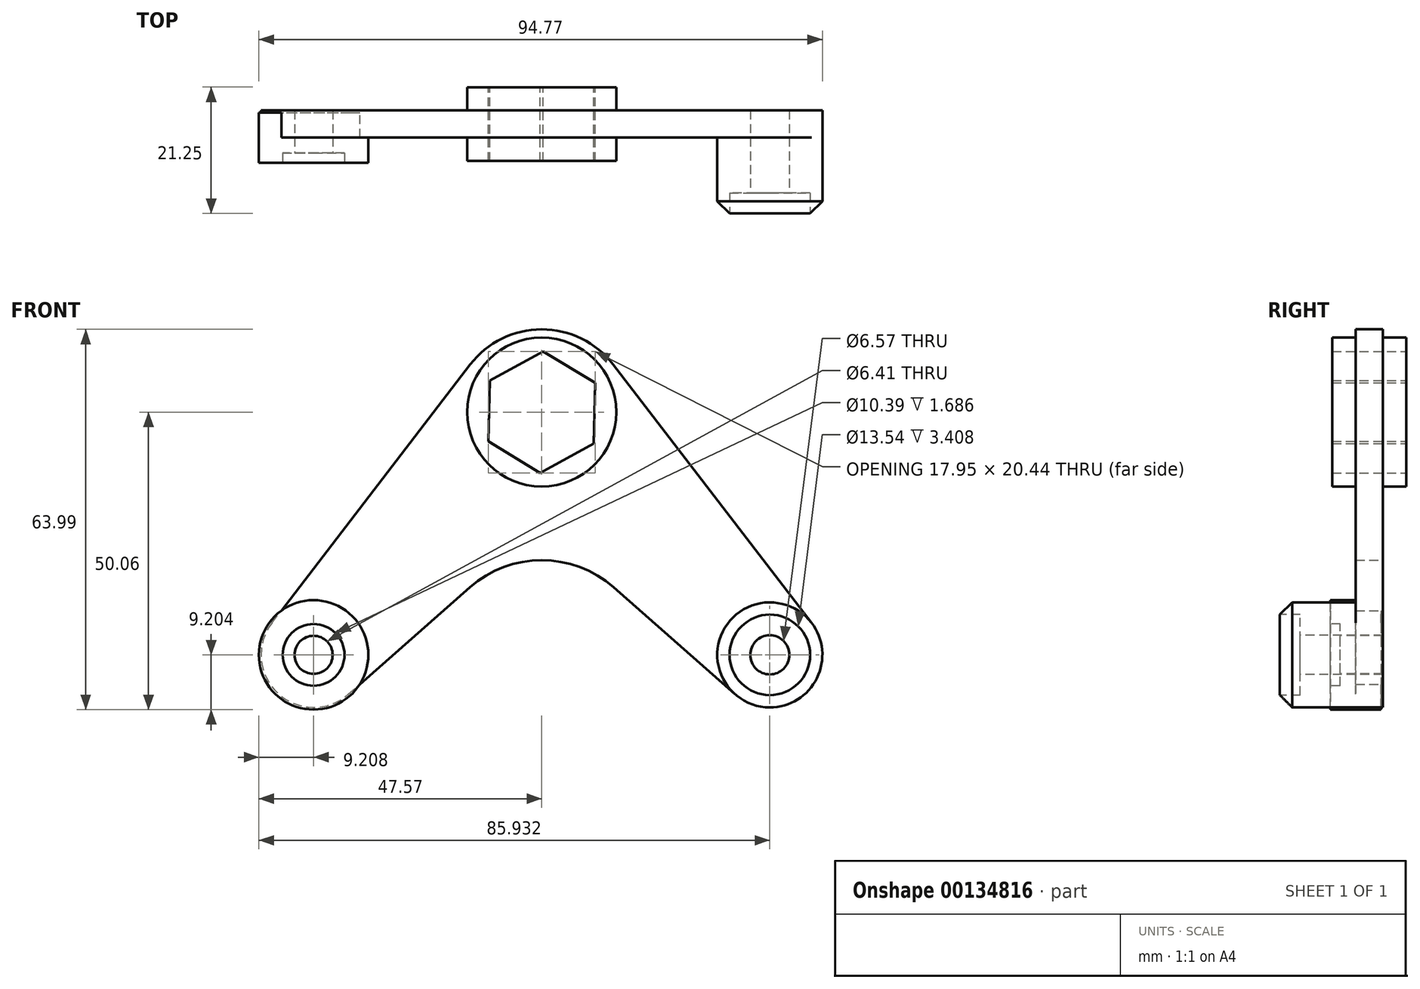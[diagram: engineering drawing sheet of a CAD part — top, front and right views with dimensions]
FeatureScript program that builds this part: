
annotation { "Feature Type Name" : "Feature", "Feature Type Description" : "" }
export const myFeature = defineFeature(function(context is Context, id is Id, definition is map)
    precondition{}
    {
        {
            var Q0;
            Q0=qCreatedBy(makeId("Front.planeOp"),FACE);
            var sketch = newSketch(context, id + "F0", { "sketchPlane" : qUnion([Q0])});
            skCircle(sketch, "E0", {"center": v(0, 0) * mm, "radius": 12.54 * mm});
            skSolve(sketch);
        }
        {
            var Q0;
            Q0 = qSketchRegion(id + "F0", true);
            extrude(context, id + "F1", {"entities" : qUnion([Q0]), "endBound" : BoundingType.SYMMETRIC, "depth" : 12.43 * mm});
        }
        {
            var Q0;
            Q0=makeQuery(id+"F1.opExtrude","CAP_FACE",FACE,{"disambiguationData":[OSD([sQuery(id+"F0.wireOp",EDGE,"E0")])],"isStart":false});
            var sketch = newSketch(context, id + "F2", { "sketchPlane" : qUnion([Q0])});
            skCircle(sketch, "E1.cCircle", {"center": v(0, 0) * mm, "radius": 7.38 * mm, "construction": true});
            skLineSegment(sketch, "E1.0", {"start": v(-8.03, 2.83) * mm, "end": v(-1.57, 8.37) * mm});
            skLineSegment(sketch, "E1.1", {"start": v(-1.57, 8.37) * mm, "end": v(6.47, 5.54) * mm});
            skLineSegment(sketch, "E1.2", {"start": v(6.47, 5.54) * mm, "end": v(8.03, -2.83) * mm});
            skLineSegment(sketch, "E1.3", {"start": v(8.03, -2.83) * mm, "end": v(1.57, -8.37) * mm});
            skLineSegment(sketch, "E1.4", {"start": v(1.57, -8.37) * mm, "end": v(-6.47, -5.54) * mm});
            skLineSegment(sketch, "E1.5", {"start": v(-6.47, -5.54) * mm, "end": v(-8.03, 2.83) * mm});
            skPoint(sketch, "E1.0.midPoint", {"position": v(-4.8, 5.6) * mm});
            skSolve(sketch);
        }
        {
            var Q0;
            Q0 = qSketchRegion(id + "F2", true);
            extrude(context, id + "F3", {"entities" : qUnion([Q0]), "operationType" : NewBodyOperationType.REMOVE, "oppositeDirection" : true, "depth" : 43.1 * mm});
        }
        {
            var Q0;
            Q0=qCreatedBy(makeId("Front.planeOp"),FACE);
            var sketch = newSketch(context, id + "F4", { "sketchPlane" : qUnion([Q0])});
            skCircle(sketch, "E2", {"center": v(-38.36, -40.86) * mm, "radius": 8.84 * mm});
            skCircle(sketch, "E3.MirrorC", {"center": v(38.36, -40.86) * mm, "radius": 8.84 * mm});
            skLineSegment(sketch, "E4", {"start": v(-45.37, -35.48) * mm, "end": v(-12, 8) * mm});
            skLineSegment(sketch, "E5.MirrorCS", {"start": v(45.37, -35.48) * mm, "end": v(12, 8) * mm});
            skLineSegment(sketch, "E6", {"start": v(-32.52, -47.49) * mm, "end": v(-12.1, -29.5) * mm});
            skLineSegment(sketch, "E7.MirrorCS", {"start": v(32.52, -47.49) * mm, "end": v(12.1, -29.5) * mm});
            skArc(sketch, "E8", {"start": v(12.1, -29.5) * mm, "mid": v(0, -24.92) * mm, "end": v(-12.1, -29.5) * mm});
            skArc(sketch, "E9", {"start": v(12, 8) * mm, "mid": v(0, 13.93) * mm, "end": v(-12, 8) * mm});
            skSolve(sketch);
        }
        {
            var Q0;
            Q0 = qSketchRegion(id + "F4", true);
            extrude(context, id + "F5", {"entities" : qUnion([Q0]), "operationType" : NewBodyOperationType.ADD, "endBound" : BoundingType.SYMMETRIC, "depth" : 4.58 * mm});
        }
        {
            var Q0;
            {var subQ0=sQuery(id+"F4.wireOp",EDGE,"E3.MirrorC");var subQ1=sQuery(id+"F4.wireOp",EDGE,"E4");var subQ2=sQuery(id+"F4.wireOp",EDGE,"E2");var subQ3=sQuery(id+"F4.wireOp",EDGE,"E8");var subQ4=sQuery(id+"F4.wireOp",EDGE,"E5.MirrorCS");var subQ5=sQuery(id+"F4.wireOp",EDGE,"E6");var subQ6=sQuery(id+"F4.wireOp",EDGE,"E9");var subQ7=sQuery(id+"F4.wireOp",EDGE,"E7.MirrorCS");Q0=makeQuery(id+"F5.boolean.opBoolean","SPLIT",FACE,{"disambiguationData":[TD([makeQuery(id+"F1.opExtrude","SWEPT_FACE",FACE,{"disambiguationData":[OSD([sQuery(id+"F0.wireOp",EDGE,"E0")])]})])],"derivedFrom":makeQuery(id+"F5.opExtrude","CAP_FACE",FACE,{"disambiguationData":[OSD([subQ2,subQ0,subQ1,subQ4,subQ5,subQ7,subQ3,subQ6])],"isStart":false})});}
            var sketch = newSketch(context, id + "F6", { "sketchPlane" : qUnion([Q0])});
            skCircle(sketch, "E10", {"center": v(-38.36, -40.86) * mm, "radius": 9.2 * mm});
            skSolve(sketch);
        }
        {
            var Q0;
            Q0 = qSketchRegion(id + "F6", true);
            extrude(context, id + "F7", {"entities" : qUnion([Q0]), "operationType" : NewBodyOperationType.ADD, "endBound" : BoundingType.SYMMETRIC, "depth" : 8.5 * mm});
        }
        {
            var Q0;
            {var subQ0=sQuery(id+"F4.wireOp",EDGE,"E3.MirrorC");var subQ1=sQuery(id+"F4.wireOp",EDGE,"E4");var subQ2=sQuery(id+"F4.wireOp",EDGE,"E2");var subQ3=sQuery(id+"F4.wireOp",EDGE,"E8");var subQ4=sQuery(id+"F4.wireOp",EDGE,"E5.MirrorCS");var subQ5=sQuery(id+"F4.wireOp",EDGE,"E6");var subQ6=sQuery(id+"F4.wireOp",EDGE,"E9");var subQ7=sQuery(id+"F4.wireOp",EDGE,"E7.MirrorCS");Q0=makeQuery(id+"F5.boolean.opBoolean","SPLIT",FACE,{"disambiguationData":[TD([makeQuery(id+"F1.opExtrude","SWEPT_FACE",FACE,{"disambiguationData":[OSD([sQuery(id+"F0.wireOp",EDGE,"E0")])]})])],"derivedFrom":makeQuery(id+"F5.opExtrude","CAP_FACE",FACE,{"disambiguationData":[OSD([subQ2,subQ0,subQ1,subQ4,subQ5,subQ7,subQ3,subQ6])],"isStart":false})});}
            var sketch = newSketch(context, id + "F8", { "sketchPlane" : qUnion([Q0])});
            skCircle(sketch, "E11", {"center": v(38.36, -40.86) * mm, "radius": 8.84 * mm});
            skSolve(sketch);
        }
        {
            var Q0;
            Q0 = qSketchRegion(id + "F8", true);
            extrude(context, id + "F9", {"entities" : qUnion([Q0]), "operationType" : NewBodyOperationType.ADD, "depth" : 13.21 * mm});
        }
        {
            var Q0;
            Q0=makeQuery(id+"F7.opExtrude","CAP_FACE",FACE,{"disambiguationData":[OSD([sQuery(id+"F6.wireOp",EDGE,"E10")])],"isStart":false});
            var sketch = newSketch(context, id + "F10", { "sketchPlane" : qUnion([Q0])});
            skCircle(sketch, "E12", {"center": v(-38.36, -40.86) * mm, "radius": 3.2 * mm});
            skSolve(sketch);
        }
        {
            var Q0;
            Q0 = qSketchRegion(id + "F10", true);
            extrude(context, id + "F11", {"entities" : qUnion([Q0]), "operationType" : NewBodyOperationType.REMOVE, "oppositeDirection" : true, "depth" : 28.8 * mm});
        }
        {
            var Q0;
            Q0=makeQuery(id+"F7.opExtrude","CAP_FACE",FACE,{"disambiguationData":[OSD([sQuery(id+"F6.wireOp",EDGE,"E10")])],"isStart":false});
            var sketch = newSketch(context, id + "F12", { "sketchPlane" : qUnion([Q0])});
            skCircle(sketch, "E13", {"center": v(-38.36, -40.86) * mm, "radius": 5.2 * mm});
            skSolve(sketch);
        }
        {
            var Q0;
            Q0 = qSketchRegion(id + "F12", true);
            extrude(context, id + "F13", {"entities" : qUnion([Q0]), "operationType" : NewBodyOperationType.REMOVE, "oppositeDirection" : true, "depth" : 1.69 * mm});
        }
        {
            var Q0;
            Q0=makeQuery(id+"F9.opExtrude","CAP_FACE",FACE,{"disambiguationData":[OSD([sQuery(id+"F8.wireOp",EDGE,"E11")])],"isStart":false});
            var sketch = newSketch(context, id + "F14", { "sketchPlane" : qUnion([Q0])});
            skCircle(sketch, "E14", {"center": v(38.36, -40.86) * mm, "radius": 3.29 * mm});
            skSolve(sketch);
        }
        {
            var Q0;
            Q0 = qSketchRegion(id + "F14", true);
            extrude(context, id + "F15", {"entities" : qUnion([Q0]), "operationType" : NewBodyOperationType.REMOVE, "oppositeDirection" : true, "depth" : 33.08 * mm});
        }
        {
            var Q0;
            Q0=makeQuery(id+"F9.opExtrude","CAP_FACE",FACE,{"disambiguationData":[OSD([sQuery(id+"F8.wireOp",EDGE,"E11")])],"isStart":false});
            var sketch = newSketch(context, id + "F16", { "sketchPlane" : qUnion([Q0])});
            skCircle(sketch, "E15", {"center": v(38.36, -40.86) * mm, "radius": 6.77 * mm});
            skSolve(sketch);
        }
        {
            var Q0;
            Q0 = qSketchRegion(id + "F16", true);
            extrude(context, id + "F17", {"entities" : qUnion([Q0]), "operationType" : NewBodyOperationType.REMOVE, "oppositeDirection" : true, "depth" : 3.88 * mm});
        }
        {
            var Q0;
            Q0=makeQuery(id+"F9.opExtrude","CAP_EDGE",EDGE,{"disambiguationData":[OSD([sQuery(id+"F8.wireOp",EDGE,"E11")])],"isStart":false});
            chamfer(context, id + "F18", {"entities" : qUnion([Q0]), "width" : 2.54 * mm, "tangentPropagation" : true});
        }
        {
            var Q0;
            Q0=makeQuery(id+"F5.boolean.opBoolean","SPLIT",FACE,{"disambiguationData":[TD([makeQuery(id+"F3.boolean.opBoolean","COPY",FACE,{"derivedFrom":makeQuery(id+"F3.opExtrude","SWEPT_FACE",FACE,{"disambiguationData":[OSD([sQuery(id+"F2.wireOp",EDGE,"E1.0")])]})})])],"derivedFrom":makeQuery(id+"F5.opExtrude","CAP_FACE",FACE,{"disambiguationData":[OSD([sQuery(id+"F4.wireOp",EDGE,"E2"),sQuery(id+"F4.wireOp",EDGE,"E3.MirrorC"),sQuery(id+"F4.wireOp",EDGE,"E4"),sQuery(id+"F4.wireOp",EDGE,"E5.MirrorCS"),sQuery(id+"F4.wireOp",EDGE,"E6"),sQuery(id+"F4.wireOp",EDGE,"E7.MirrorCS"),sQuery(id+"F4.wireOp",EDGE,"E8"),sQuery(id+"F4.wireOp",EDGE,"E9")])],"isStart":false})});
            var sketch = newSketch(context, id + "F19", { "sketchPlane" : qUnion([Q0])});
            skCircle(sketch, "E16.cCircle", {"center": v(0, 0) * mm, "radius": 7.5 * mm, "construction": true});
            skLineSegment(sketch, "E16.0", {"start": v(7.5, 4.33) * mm, "end": v(7.5, -4.33) * mm});
            skLineSegment(sketch, "E16.1", {"start": v(7.5, -4.33) * mm, "end": v(0, -8.67) * mm});
            skLineSegment(sketch, "E16.2", {"start": v(0, -8.67) * mm, "end": v(-7.5, -4.33) * mm});
            skLineSegment(sketch, "E16.3", {"start": v(-7.5, -4.33) * mm, "end": v(-7.5, 4.33) * mm});
            skLineSegment(sketch, "E16.4", {"start": v(-7.5, 4.33) * mm, "end": v(0, 8.67) * mm});
            skLineSegment(sketch, "E16.5", {"start": v(0, 8.67) * mm, "end": v(7.5, 4.33) * mm});
            skPoint(sketch, "E16.0.midPoint", {"position": v(7.5, 0) * mm});
            skSolve(sketch);
        }
        {
            var Q0;
            Q0 = qSketchRegion(id + "F19", true);
            extrude(context, id + "F20", {"entities" : qUnion([Q0]), "operationType" : NewBodyOperationType.REMOVE, "oppositeDirection" : true, "depth" : 42.8 * mm});
        }
        {
            var Q0;
            Q0=qCreatedBy(makeId("Front.planeOp"),FACE);
            var sketch = newSketch(context, id + "F21", { "sketchPlane" : qUnion([Q0])});
            skCircle(sketch, "E17.cCircle", {"center": v(0, 0) * mm, "radius": 8.85 * mm, "construction": true});
            skLineSegment(sketch, "E17.0", {"start": v(0.25, 10.22) * mm, "end": v(8.98, 4.9) * mm});
            skLineSegment(sketch, "E17.1", {"start": v(8.98, 4.9) * mm, "end": v(8.73, -5.32) * mm});
            skLineSegment(sketch, "E17.2", {"start": v(8.73, -5.32) * mm, "end": v(-0.25, -10.22) * mm});
            skLineSegment(sketch, "E17.3", {"start": v(-0.25, -10.22) * mm, "end": v(-8.98, -4.9) * mm});
            skLineSegment(sketch, "E17.4", {"start": v(-8.98, -4.9) * mm, "end": v(-8.73, 5.32) * mm});
            skLineSegment(sketch, "E17.5", {"start": v(-8.73, 5.32) * mm, "end": v(0.25, 10.22) * mm});
            skPoint(sketch, "E17.0.midPoint", {"position": v(4.61, 7.56) * mm});
            skSolve(sketch);
        }
        {
            var Q0;
            Q0 = qSketchRegion(id + "F21", true);
            extrude(context, id + "F22", {"entities" : qUnion([Q0]), "operationType" : NewBodyOperationType.REMOVE, "endBound" : BoundingType.SYMMETRIC, "depth" : 25 * mm});
        }
    });
